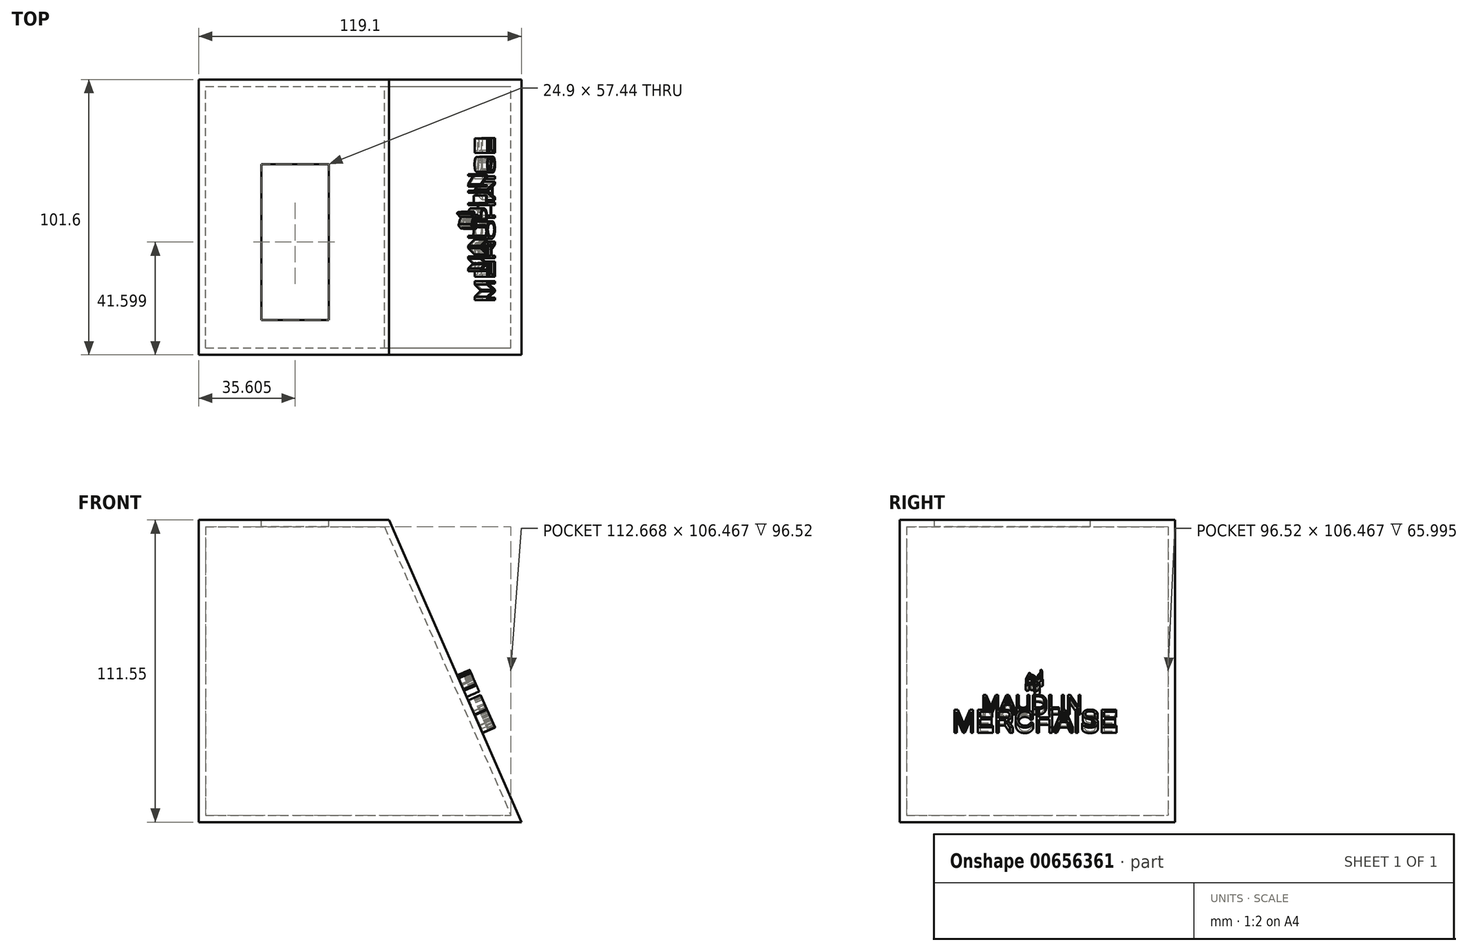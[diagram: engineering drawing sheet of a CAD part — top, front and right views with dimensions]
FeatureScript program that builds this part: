
annotation { "Feature Type Name" : "Feature", "Feature Type Description" : "" }
export const myFeature = defineFeature(function(context is Context, id is Id, definition is map)
    precondition{}
    {
        {
            var Q0;
            Q0=qCreatedBy(makeId("Front.planeOp"),FACE);
            var sketch = newSketch(context, id + "F0", { "sketchPlane" : qUnion([Q0])});
            skLineSegment(sketch, "E0", {"start": v(-35.36, 0) * mm, "end": v(34.84, 0) * mm});
            skLineSegment(sketch, "E1", {"start": v(-35.36, 0) * mm, "end": v(-35.36, -111.55) * mm});
            skLineSegment(sketch, "E2", {"start": v(-35.36, -111.55) * mm, "end": v(83.74, -111.55) * mm});
            skLineSegment(sketch, "E3", {"start": v(34.84, 0) * mm, "end": v(83.74, -111.55) * mm});
            skSolve(sketch);
        }
        {
            var Q0;
            Q0=qCreatedBy(makeId("Top.planeOp"),FACE);
            var sketch = newSketch(context, id + "F1", { "sketchPlane" : qUnion([Q0])});
            skLineSegment(sketch, "E4.bottom", {"start": v(12.7, -31.28) * mm, "end": v(-12.2, -31.28) * mm});
            skLineSegment(sketch, "E4.top", {"start": v(12.7, -88.72) * mm, "end": v(-12.2, -88.72) * mm});
            skLineSegment(sketch, "E4.left", {"start": v(12.7, -31.28) * mm, "end": v(12.7, -88.72) * mm});
            skLineSegment(sketch, "E4.right", {"start": v(-12.2, -31.28) * mm, "end": v(-12.2, -88.72) * mm});
            skSolve(sketch);
        }
        {
            var Q0;
            Q0 = qSketchRegion(id + "F0", true);
            extrude(context, id + "F2", {"entities" : qUnion([Q0]), "depth" : 101.6 * mm, "offsetDistance" : 25.4 * mm});
        }
        {
            var Q0;
            Q0=makeQuery(id+"F1.imprint","IMPRINT",FACE,{"disambiguationData":[TD([[makeQuery(id+"F1.imprint","IMPRINT",EDGE,{"derivedFrom":sQuery(id+"F1.wireOp",EDGE,"E4.bottom")}),1.0]])]});
            extrude(context, id + "F3", {"entities" : qUnion([Q0]), "operationType" : NewBodyOperationType.REMOVE, "oppositeDirection" : true, "depth" : 104.9 * mm, "offsetDistance" : 25.4 * mm});
        }
        {
            var Q0;
            Q0=makeQuery(id+"F3.boolean.opBoolean","COPY",FACE,{"derivedFrom":makeQuery(id+"F3.opExtrude","SWEPT_FACE",FACE,{"disambiguationData":[OSD([sQuery(id+"F1.wireOp",EDGE,"E4.left")])]})});
            var Q1;
            Q1=makeQuery(id+"F3.boolean.opBoolean","COPY",FACE,{"derivedFrom":makeQuery(id+"F3.opExtrude","SWEPT_FACE",FACE,{"disambiguationData":[OSD([sQuery(id+"F1.wireOp",EDGE,"E4.top")])]})});
            var Q2;
            Q2=makeQuery(id+"F3.boolean.opBoolean","COPY",FACE,{"derivedFrom":makeQuery(id+"F3.opExtrude","CAP_FACE",FACE,{"disambiguationData":[OSD([sQuery(id+"F1.wireOp",EDGE,"E4.bottom"),sQuery(id+"F1.wireOp",EDGE,"E4.top"),sQuery(id+"F1.wireOp",EDGE,"E4.left"),sQuery(id+"F1.wireOp",EDGE,"E4.right")])],"isStart":false})});
            var Q3;
            Q3=makeQuery(id+"F3.boolean.opBoolean","COPY",FACE,{"derivedFrom":makeQuery(id+"F3.opExtrude","SWEPT_FACE",FACE,{"disambiguationData":[OSD([sQuery(id+"F1.wireOp",EDGE,"E4.bottom")])]})});
            var Q4;
            Q4=makeQuery(id+"F3.boolean.opBoolean","COPY",FACE,{"derivedFrom":makeQuery(id+"F3.opExtrude","SWEPT_FACE",FACE,{"disambiguationData":[OSD([sQuery(id+"F1.wireOp",EDGE,"E4.right")])]})});
            shell(context, id + "F4", {"entities" : qUnion([Q0, Q1, Q2, Q3, Q4]), "thickness" : 2.54 * mm});
        }
        {
            var Q0;
            Q0=makeQuery(id+"F2.opExtrude","SWEPT_FACE",FACE,{"disambiguationData":[OSD([sQuery(id+"F0.wireOp",EDGE,"E3")])]});
            var sketch = newSketch(context, id + "F5", { "sketchPlane" : qUnion([Q0])});
            skText(sketch, "E5", { "text": "MERCHAISE", "fontName": "Arimo-Regular.ttf"});
            skText(sketch, "E6", { "text": "MAUDLIN", "fontName": "Arimo-Regular.ttf"});
            skFitSpline(sketch, "E7", {"points": [v(-55.1, -82.37) * mm, v(-54.75, -82.41) * mm, v(-54.4, -82.24) * mm, v(-54.26, -81.71) * mm, v(-54.22, -81.3) * mm, v(-54.47, -80.97) * mm, v(-54.72, -80.81) * mm, v(-54.5, -80.7) * mm, v(-54.89, -80.43) * mm, v(-54.93, -80.13) * mm, v(-54.9, -79.87) * mm, v(-54.7, -79.6) * mm, v(-54.6, -79.27) * mm, v(-54.37, -78.93) * mm, v(-54.12, -78.49) * mm, v(-54.02, -78.1) * mm, v(-53.85, -77.95) * mm, v(-53.55, -77.93) * mm, v(-53.34, -78.33) * mm], "startDerivative": vector(6.17, -1.46) * mm, "endDerivative": vector(2.64, -8.23) * mm});
            skFitSpline(sketch, "E8", {"points": [v(-53.34, -78.33) * mm, v(-52.94, -78.54) * mm, v(-52.46, -78.73) * mm, v(-52.06, -78.94) * mm, v(-51.72, -79.14) * mm, v(-51.5, -79.4) * mm, v(-51.22, -79.73) * mm, v(-51, -80.06) * mm, v(-50.83, -80.18) * mm, v(-50.8, -80.44) * mm, v(-50.74, -80.63) * mm, v(-50.63, -80.69) * mm, v(-50.6, -80.27) * mm, v(-50.7, -79.9) * mm, v(-50.7, -79.46) * mm, v(-50.66, -79.03) * mm, v(-50.47, -78.6) * mm, v(-50.19, -78.33) * mm, v(-49.92, -78.05) * mm, v(-49.74, -77.76) * mm, v(-49.69, -77.24) * mm], "startDerivative": vector(6.9, -4.09) * mm, "endDerivative": vector(0.24, 9.5) * mm});
            skFitSpline(sketch, "E9", {"points": [v(-49.69, -77.24) * mm, v(-49.69, -76.82) * mm, v(-49.44, -76.64) * mm, v(-49.16, -76.7) * mm, v(-49.07, -77.24) * mm, v(-48.96, -77.64) * mm], "startDerivative": vector(-0.35, 2.22) * mm, "endDerivative": vector(0.71, -1.76) * mm});
            skFitSpline(sketch, "E10", {"points": [v(-48.96, -77.64) * mm, v(-49.16, -78.13) * mm, v(-48.96, -78.65) * mm], "startDerivative": vector(-0.63, -0.98) * mm, "endDerivative": vector(0.62, -1.02) * mm});
            skFitSpline(sketch, "E11", {"points": [v(-48.96, -78.65) * mm, v(-49.4, -78.9) * mm, v(-49.8, -79.06) * mm, v(-49.84, -79.38) * mm, v(-49.92, -79.89) * mm, v(-49.94, -80.23) * mm, v(-49.63, -80.15) * mm, v(-49.24, -80.17) * mm, v(-48.96, -80.37) * mm, v(-48.79, -80.6) * mm, v(-48.96, -80.95) * mm, v(-49.36, -81.04) * mm, v(-49.63, -81.23) * mm, v(-49.93, -81.57) * mm, v(-50.03, -82.07) * mm, v(-50, -82.68) * mm, v(-49.88, -83.15) * mm, v(-49.94, -83.69) * mm, v(-50.11, -84.35) * mm, v(-50.51, -84.87) * mm, v(-51.05, -85.3) * mm, v(-51.7, -85.29) * mm, v(-51.84, -84.95) * mm, v(-51.52, -84.89) * mm, v(-51.38, -84.43) * mm, v(-51.54, -84.22) * mm, v(-51.66, -84) * mm, v(-51.62, -83.51) * mm, v(-51.9, -83.31) * mm, v(-52.06, -83.02) * mm, v(-52.1, -82.6) * mm, v(-52.77, -82.63) * mm, v(-53.18, -82.57) * mm, v(-53.39, -82.3) * mm, v(-53.56, -81.9) * mm, v(-53.75, -81.9) * mm, v(-53.76, -82.46) * mm, v(-54.3, -82.77) * mm, v(-54.81, -82.85) * mm, v(-54.95, -82.66) * mm, v(-55.1, -82.37) * mm], "startDerivative": vector(-15.1, -10.97) * mm, "endDerivative": vector(-7, 13.6) * mm});
            skFitSpline(sketch, "E12", {"points": [v(-54.18, -80.18) * mm, v(-54.1, -79.93) * mm, v(-53.95, -79.69) * mm, v(-53.84, -79.48) * mm, v(-53.7, -79.23) * mm, v(-53.46, -79.1) * mm, v(-53.25, -79.2) * mm, v(-53.2, -79.31) * mm, v(-53.18, -79.13) * mm, v(-53.04, -79.05) * mm, v(-52.85, -79.04) * mm, v(-52.57, -79.1) * mm, v(-52.36, -79.24) * mm, v(-52.15, -79.45) * mm, v(-51.94, -79.6) * mm, v(-51.66, -79.81) * mm, v(-51.37, -80.04) * mm, v(-51.4, -80.22) * mm, v(-51.6, -80.13) * mm, v(-51.79, -80.02) * mm, v(-51.94, -79.81) * mm, v(-52.34, -79.72) * mm, v(-52.72, -79.76) * mm, v(-53.04, -79.88) * mm, v(-53.3, -80.1) * mm, v(-53.52, -80.33) * mm, v(-53.69, -80.5) * mm, v(-53.91, -80.5) * mm, v(-54.05, -80.43) * mm, v(-54.18, -80.18) * mm]});
            skFitSpline(sketch, "E13", {"points": [v(-53.13, -80.68) * mm, v(-53.2, -80.45) * mm, v(-53.1, -80.29) * mm, v(-52.87, -80.18) * mm, v(-52.57, -80.13) * mm, v(-52.3, -80.19) * mm, v(-52.07, -80.26) * mm, v(-51.74, -80.4) * mm, v(-51.5, -80.54) * mm, v(-51.69, -80.76) * mm, v(-51.8, -80.81) * mm, v(-51.73, -81.06) * mm, v(-51.5, -81.15) * mm, v(-51.2, -81.37) * mm, v(-50.96, -81.38) * mm, v(-50.77, -81.5) * mm, v(-50.73, -81.73) * mm, v(-50.78, -82.2) * mm, v(-50.75, -82.65) * mm, v(-50.77, -82.98) * mm, v(-50.92, -83.16) * mm, v(-50.97, -82.98) * mm, v(-51.2, -82.77) * mm, v(-51.48, -82.63) * mm, v(-51.57, -82.41) * mm, v(-51.73, -82.32) * mm, v(-51.88, -82.43) * mm, v(-52.08, -82.34) * mm, v(-51.87, -82.07) * mm, v(-51.85, -81.97) * mm], "startDerivative": vector(-3.72, 6.97) * mm, "endDerivative": vector(-1.01, 4.03) * mm});
            skFitSpline(sketch, "E14", {"points": [v(-51.97, -81.86) * mm, v(-52.17, -81.86) * mm, v(-52.31, -82.04) * mm, v(-52.5, -82.16) * mm, v(-52.77, -82.13) * mm, v(-52.97, -81.98) * mm, v(-53.11, -81.9) * mm, v(-53.14, -81.7) * mm, v(-53.05, -81.45) * mm, v(-52.8, -81.3) * mm, v(-52.7, -81.12) * mm, v(-52.62, -80.98) * mm, v(-52.55, -80.8) * mm, v(-52.57, -80.6) * mm, v(-52.72, -80.55) * mm, v(-52.93, -80.65) * mm, v(-53.13, -80.68) * mm], "startDerivative": vector(-3.68, 0.76) * mm, "endDerivative": vector(-3.2, -0.07) * mm});
            skFitSpline(sketch, "E15", {"points": [v(-53.1, -80.7) * mm, v(-53.06, -80.67) * mm], "startDerivative": vector(0.04, 0.03) * mm, "endDerivative": vector(0.04, 0.03) * mm});
            skFitSpline(sketch, "E16", {"points": [v(-51.97, -81.86) * mm, v(-51.85, -82) * mm], "startDerivative": vector(0.12, -0.14) * mm, "endDerivative": vector(0.12, -0.14) * mm});
            const initialGuessF5  = {"E5": [-0.0822, -0.09983, 1, 0, 0.0074], "E6": [-0.07143, -0.09243, 1, 0, 0.00595]};
            skSetInitialGuess(sketch, initialGuessF5);
            skSolve(sketch);
        }
        {
            var Q0;
            Q0=makeQuery(id+"F5.imprint","IMPRINT",FACE,{"disambiguationData":[TD([[makeQuery(id+"F5.imprint","IMPRINT",EDGE,{"derivedFrom":sQuery(id+"F5.wireOp",EDGE,"E7")}),-1.0]])]});
            var Q1;
            Q1 = qSketchRegion(id + "F5", true);
            extrude(context, id + "F6", {"entities" : qUnion([Q0, Q1]), "operationType" : NewBodyOperationType.ADD, "depth" : 5.08 * mm, "offsetDistance" : 25.4 * mm});
        }
    });
